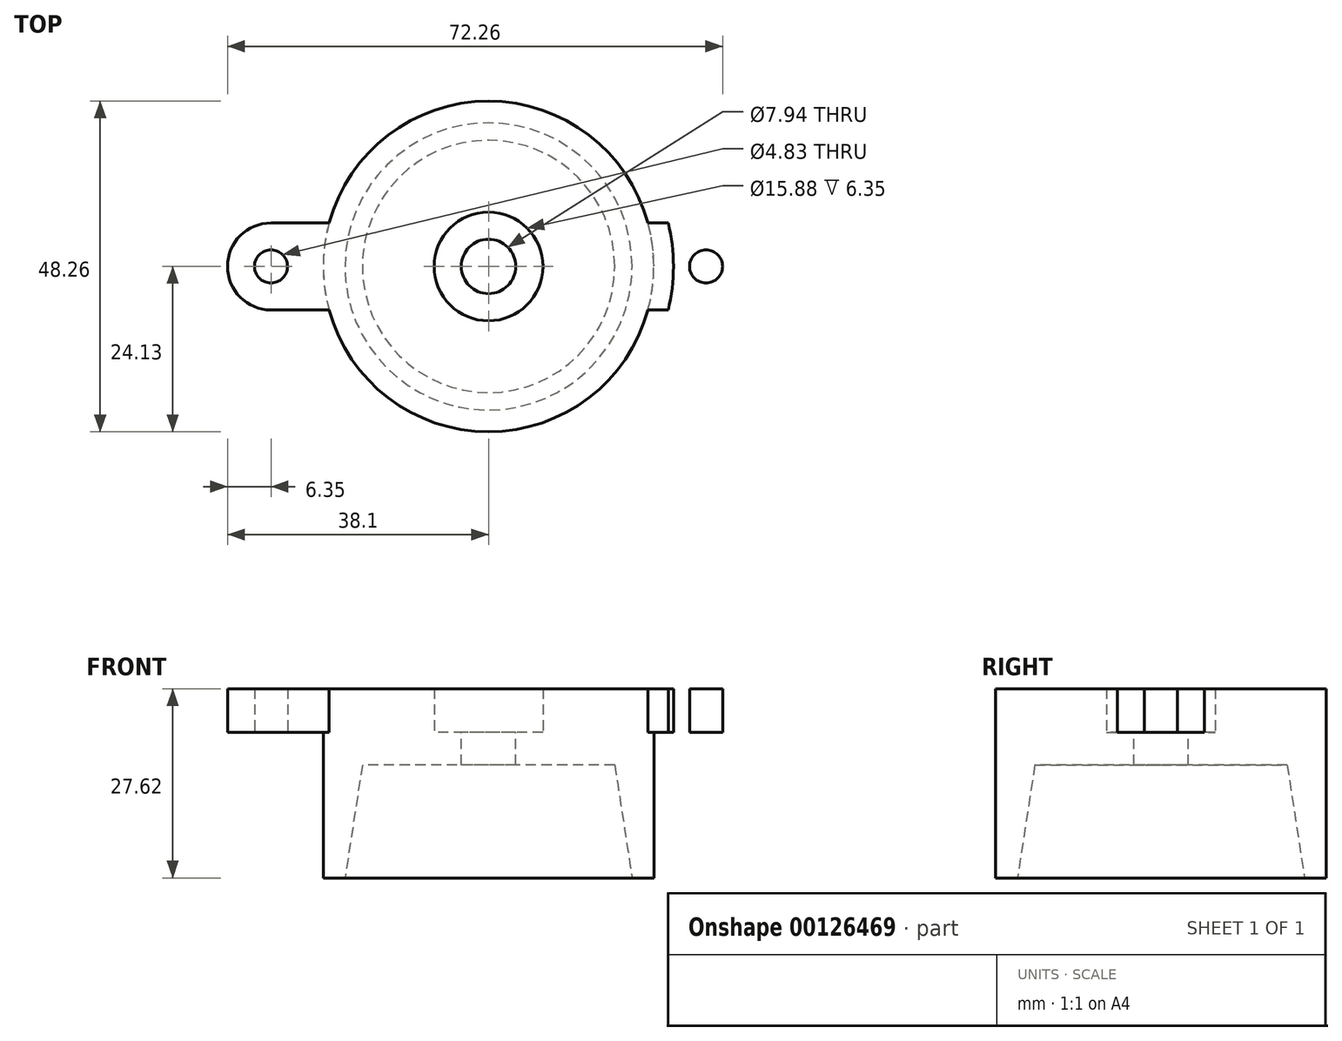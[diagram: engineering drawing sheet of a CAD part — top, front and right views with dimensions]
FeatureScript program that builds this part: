
annotation { "Feature Type Name" : "Feature", "Feature Type Description" : "" }
export const myFeature = defineFeature(function(context is Context, id is Id, definition is map)
    precondition{}
    {
        {
            var Q0;
            Q0=qCreatedBy(makeId("Top.planeOp"),FACE);
            var sketch = newSketch(context, id + "F0", { "sketchPlane" : qUnion([Q0])});
            skCircle(sketch, "E0", {"center": v(0, 0) * mm, "radius": 20.96 * mm});
            skCircle(sketch, "E1", {"center": v(0, 0) * mm, "radius": 24.13 * mm});
            skSolve(sketch);
        }
        {
            var Q0;
            Q0=makeQuery(id+"F0.imprint","IMPRINT",FACE,{"disambiguationData":[TD([[makeQuery(id+"F0.imprint","IMPRINT",EDGE,{"derivedFrom":sQuery(id+"F0.wireOp",EDGE,"E0")}),1.0]])]});
            var Q1;
            Q1=makeQuery(id+"F0.imprint","IMPRINT",FACE,{"disambiguationData":[TD([[makeQuery(id+"F0.imprint","IMPRINT",EDGE,{"derivedFrom":sQuery(id+"F0.wireOp",EDGE,"E0")}),-1.0]])]});
            extrude(context, id + "F1", {"entities" : qUnion([Q0, Q1]), "depth" : 16.5 * mm});
        }
        {
            var Q0;
            Q0=makeQuery(id+"F1.opExtrude","CAP_FACE",FACE,{"disambiguationData":[OSD([sQuery(id+"F0.wireOp",EDGE,"E1")])],"isStart":false});
            var sketch = newSketch(context, id + "F2", { "sketchPlane" : qUnion([Q0])});
            skCircle(sketch, "E2", {"center": v(0, 0) * mm, "radius": 18.41 * mm});
            skSolve(sketch);
        }
        {
            var Q1;
            Q1=makeQuery(id+"F0.imprint","IMPRINT",FACE,{"disambiguationData":[TD([[makeQuery(id+"F0.imprint","IMPRINT",EDGE,{"derivedFrom":sQuery(id+"F0.wireOp",EDGE,"E0")}),1.0]])]});
            var Q2;
            Q2=makeQuery(id+"F2.imprint","IMPRINT",FACE,{"disambiguationData":[TD([[makeQuery(id+"F2.imprint","IMPRINT",EDGE,{"derivedFrom":sQuery(id+"F2.wireOp",EDGE,"E2")}),1.0]])]});
            loft(context, id + "F3", {"operationType" : NewBodyOperationType.REMOVE, "sheetProfilesArray" : [{ "sheetProfileEntities" : qUnion([Q1]) }, { "sheetProfileEntities" : qUnion([Q2]) }]});
        }
        {
            var Q0;
            Q0=makeQuery(id+"F2.imprint","IMPRINT",FACE,{"disambiguationData":[TD([[makeQuery(id+"F2.imprint","IMPRINT",EDGE,{"derivedFrom":sQuery(id+"F2.wireOp",EDGE,"E2")}),-1.0]])]});
            var Q1;
            Q1=makeQuery(id+"F2.imprint","IMPRINT",FACE,{"disambiguationData":[TD([[makeQuery(id+"F2.imprint","IMPRINT",EDGE,{"derivedFrom":sQuery(id+"F2.wireOp",EDGE,"E2")}),1.0]])]});
            extrude(context, id + "F4", {"entities" : qUnion([Q0, Q1]), "operationType" : NewBodyOperationType.ADD, "depth" : 4.76 * mm});
        }
        {
            var Q0;
            Q0=makeQuery(id+"F4.opExtrude","CAP_FACE",FACE,{"disambiguationData":[OSD([sQuery(id+"F0.wireOp",EDGE,"E1")])],"isStart":false});
            var sketch = newSketch(context, id + "F5", { "sketchPlane" : qUnion([Q0])});
            skCircle(sketch, "E3", {"center": v(0, 0) * mm, "radius": 3.97 * mm});
            skCircle(sketch, "E4", {"center": v(0, 0) * mm, "radius": 7.94 * mm});
            skPoint(sketch, "E5", {"position": v(-31.75, 0) * mm});
            skCircle(sketch, "E6", {"center": v(-31.75, 0) * mm, "radius": 2.41 * mm});
            skLineSegment(sketch, "E7", {"start": v(-31.75, 0) * mm, "end": v(0, 0) * mm, "construction": true});
            skLineSegment(sketch, "E8", {"start": v(0, 0) * mm, "end": v(0, 37.77) * mm, "construction": true});
            skCircle(sketch, "E9.MirrorC", {"center": v(31.75, 0) * mm, "radius": 2.41 * mm});
            skLineSegment(sketch, "E10", {"start": v(-31.75, 0) * mm, "end": v(-31.75, 11.45) * mm, "construction": true});
            skLineSegment(sketch, "E11", {"start": v(-31.75, 6.35) * mm, "end": v(-23.28, 6.35) * mm});
            skArc(sketch, "E12", {"start": v(-31.75, 6.35) * mm, "mid": v(-38.1, 0) * mm, "end": v(-31.75, -6.35) * mm});
            skLineSegment(sketch, "E13.MirrorCS", {"start": v(-31.75, -6.35) * mm, "end": v(-23.28, -6.35) * mm});
            skLineSegment(sketch, "E14.MirrorCS", {"start": v(31.75, 6.35) * mm, "end": v(23.28, 6.35) * mm});
            skArc(sketch, "E15.MirrorCS", {"start": v(31.75, 6.35) * mm, "mid": v(38.1, 0) * mm, "end": v(31.75, -6.35) * mm});
            skLineSegment(sketch, "E16.MirrorCS", {"start": v(31.75, -6.35) * mm, "end": v(23.28, -6.35) * mm});
            skArc(sketch, "E17", {"start": v(-26.23, 6.35) * mm, "mid": v(-26.99, 0) * mm, "end": v(-26.23, -6.35) * mm});
            skArc(sketch, "E18.trimOffspring", {"start": v(26.23, -6.35) * mm, "mid": v(26.99, 0) * mm, "end": v(26.23, 6.35) * mm});
            skSolve(sketch);
        }
        {
            var Q0;
            Q0=makeQuery(id+"F5.imprint","IMPRINT",FACE,{"disambiguationData":[TD([[makeQuery(id+"F5.imprint","IMPRINT",EDGE,{"derivedFrom":sQuery(id+"F5.wireOp",EDGE,"E3")}),1.0]])]});
            var Q1;
            Q1=sQuery(id+"F5.wireOp",EDGE,"E3");
            var Q2;
            Q2=makeQuery(id+"F4.opExtrude","CAP_FACE",FACE,{"disambiguationData":[OSD([sQuery(id+"F0.wireOp",EDGE,"E1")])],"isStart":true});
            extrude(context, id + "F6", {"entities" : qUnion([Q0]), "operationType" : NewBodyOperationType.REMOVE, "surfaceEntities" : qUnion([Q1]), "endBound" : BoundingType.UP_TO_SURFACE, "oppositeDirection" : true, "endBoundEntityFace" : qUnion([Q2]), "depth" : 25.4 * mm});
        }
        {
            var Q0;
            Q0=makeQuery(id+"F5.imprint","IMPRINT",FACE,{"disambiguationData":[TD([[makeQuery(id+"F5.imprint","IMPRINT",EDGE,{"derivedFrom":sQuery(id+"F5.wireOp",EDGE,"E6")}),-1.0]])]});
            var Q1;
            Q1=makeQuery(id+"F5.imprint","IMPRINT",FACE,{"disambiguationData":[TD([[makeQuery(id+"F5.imprint","IMPRINT",EDGE,{"derivedFrom":sQuery(id+"F5.wireOp",EDGE,"E4")}),-1.0]])]});
            var Q2;
            {var subQ1=sQuery(id+"F5.wireOp",EDGE,"c6da6974-5d51-4555-bfad-a0aed7c0d0f90.MirrorCS");Q2=makeQuery(id+"F5.imprint","IMPRINT",FACE,{"disambiguationData":[TD([[makeQuery(id+"F5.imprint","IMPRINT",EDGE,{"derivedFrom":subQ1}),1.0]])]});}
            var Q3;
            Q3=makeQuery(id+"F5.imprint","IMPRINT",FACE,{"disambiguationData":[TD([[makeQuery(id+"F5.imprint","IMPRINT",EDGE,{"derivedFrom":sQuery(id+"F5.wireOp",EDGE,"E9.MirrorC")}),1.0]])]});
            var Q4;
            {var subQ3=sQuery(id+"F5.wireOp",EDGE,"E17");Q4=makeQuery(id+"F5.imprint","IMPRINT",FACE,{"disambiguationData":[TD([[makeQuery(id+"F5.imprint","IMPRINT",EDGE,{"derivedFrom":subQ3}),1.0]])]});}
            var Q5;
            {var subQ3=sQuery(id+"F5.wireOp",EDGE,"E18.trimOffspring");Q5=makeQuery(id+"F5.imprint","IMPRINT",FACE,{"disambiguationData":[TD([[makeQuery(id+"F5.imprint","IMPRINT",EDGE,{"derivedFrom":subQ3}),1.0]])]});}
            extrude(context, id + "F7", {"entities" : qUnion([Q0, Q1, Q2, Q3, Q4, Q5]), "operationType" : NewBodyOperationType.ADD, "depth" : 6.35 * mm});
        }
    });
